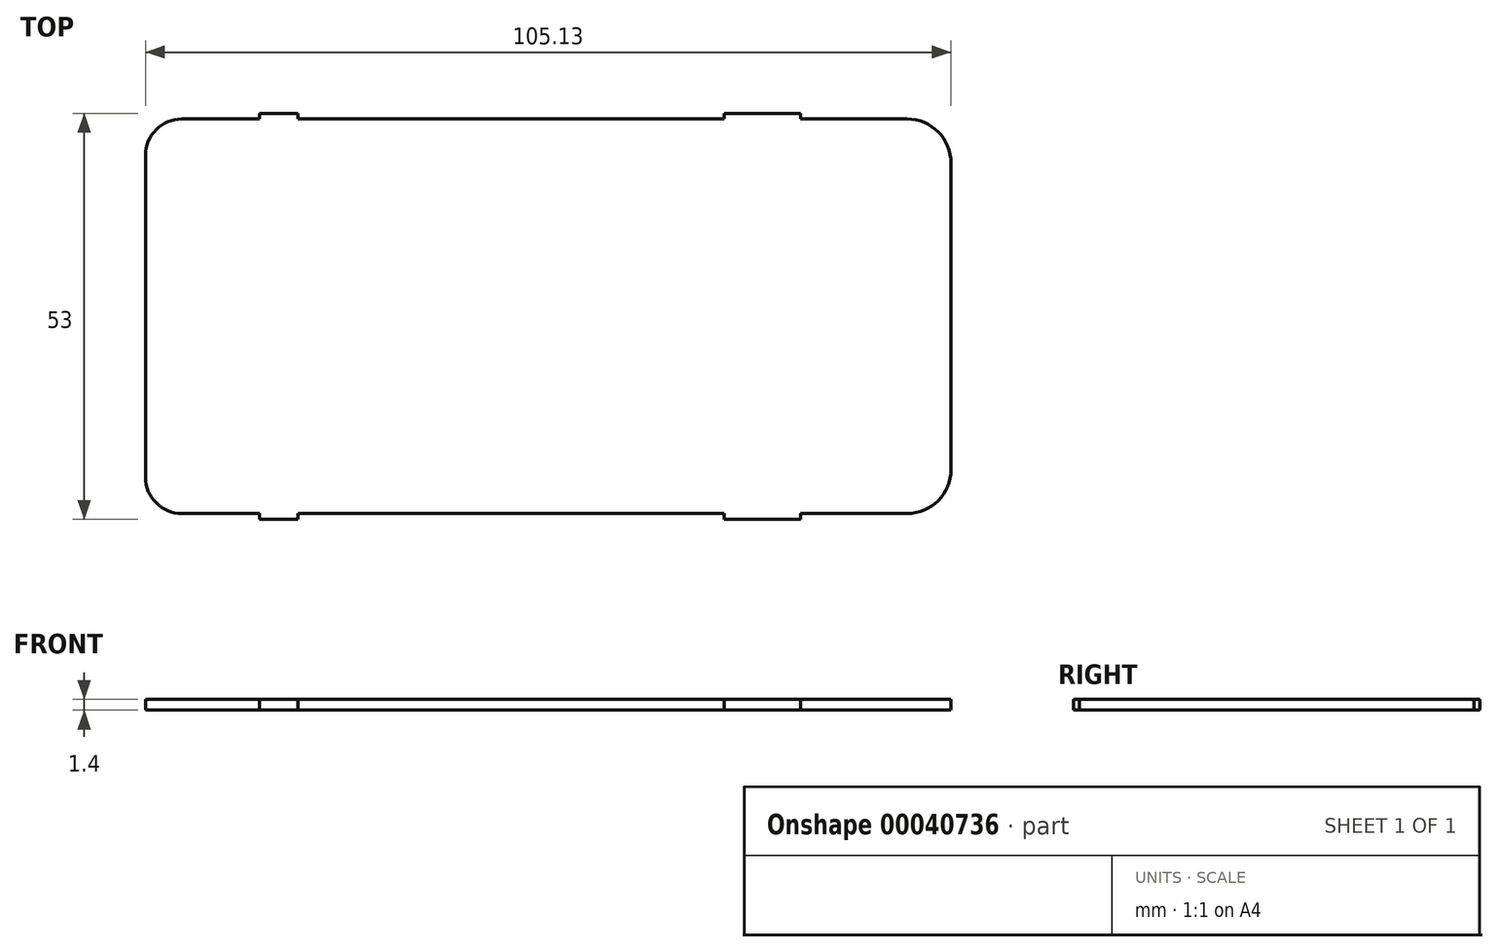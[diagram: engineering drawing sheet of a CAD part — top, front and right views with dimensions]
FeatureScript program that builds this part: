
annotation { "Feature Type Name" : "Feature", "Feature Type Description" : "" }
export const myFeature = defineFeature(function(context is Context, id is Id, definition is map)
    precondition{}
    {
        {
            var Q0;
            Q0=qCreatedBy(makeId("Top.planeOp"),FACE);
            var sketch = newSketch(context, id + "F0", { "sketchPlane" : qUnion([Q0])});
            skLineSegment(sketch, "E0", {"start": v(-46.45, 26.5) * mm, "end": v(-46.45, 25) * mm});
            skLineSegment(sketch, "E1", {"start": v(-46.45, -26.5) * mm, "end": v(-46.45, -25) * mm});
            skLineSegment(sketch, "E2", {"start": v(-50.45, -21) * mm, "end": v(-51.95, -21) * mm});
            skLineSegment(sketch, "E3", {"start": v(-50.45, 21) * mm, "end": v(-51.95, 21) * mm});
            skLineSegment(sketch, "E4", {"start": v(48.18, 25) * mm, "end": v(48.18, 26.5) * mm});
            skLineSegment(sketch, "E5", {"start": v(53.18, 20) * mm, "end": v(54.68, 20) * mm});
            skLineSegment(sketch, "E6", {"start": v(54.68, -20) * mm, "end": v(53.18, -20) * mm});
            skLineSegment(sketch, "E7", {"start": v(48.18, -26.5) * mm, "end": v(48.18, -25) * mm});
            skLineSegment(sketch, "E8", {"start": v(-46.45, -25.75) * mm, "end": v(48.18, -25.75) * mm});
            skLineSegment(sketch, "E9", {"start": v(-46.45, 25.75) * mm, "end": v(48.18, 25.75) * mm});
            skLineSegment(sketch, "E10", {"start": v(-51.2, 21) * mm, "end": v(-51.2, -21) * mm});
            skArc(sketch, "E11", {"start": v(-51.2, 21) * mm, "mid": v(-49.81, 24.36) * mm, "end": v(-46.45, 25.75) * mm});
            skArc(sketch, "E12", {"start": v(-51.2, -21) * mm, "mid": v(-49.81, -24.36) * mm, "end": v(-46.45, -25.75) * mm});
            skLineSegment(sketch, "E13", {"start": v(53.93, 20) * mm, "end": v(53.93, -20) * mm});
            skArc(sketch, "E14", {"start": v(48.18, -25.75) * mm, "mid": v(52.24, -24.07) * mm, "end": v(53.93, -20) * mm});
            skArc(sketch, "E15", {"start": v(53.93, 20) * mm, "mid": v(52.24, 24.07) * mm, "end": v(48.18, 25.75) * mm});
            skLineSegment(sketch, "E16", {"start": v(-36.31, 26.5) * mm, "end": v(-36.31, -26.5) * mm});
            skLineSegment(sketch, "E17", {"start": v(-36.31, -26.5) * mm, "end": v(-31.31, -26.5) * mm});
            skLineSegment(sketch, "E18", {"start": v(-31.31, -26.5) * mm, "end": v(-31.31, 26.5) * mm});
            skLineSegment(sketch, "E19", {"start": v(-31.31, 26.5) * mm, "end": v(-36.31, 26.5) * mm});
            skLineSegment(sketch, "E20", {"start": v(24.3, 26.5) * mm, "end": v(24.3, -26.5) * mm});
            skLineSegment(sketch, "E21", {"start": v(24.3, -26.5) * mm, "end": v(34.3, -26.5) * mm});
            skLineSegment(sketch, "E22", {"start": v(34.3, -26.5) * mm, "end": v(34.3, 26.5) * mm});
            skLineSegment(sketch, "E23", {"start": v(34.3, 26.5) * mm, "end": v(24.3, 26.5) * mm});
            skSolve(sketch);
        }
        {
            var Q0;
            {var subQ3=sQuery(id+"F0.wireOp",EDGE,"E8");var subQ5=sQuery(id+"F0.wireOp",EDGE,"E18");var subQ7=makeQuery(id+"F0.imprint","INTERSECT",VERTEX,{"derivedFrom":[subQ3,subQ5]});Q0=makeQuery(id+"F0.imprint","IMPRINT",FACE,{"disambiguationData":[TD([[makeQuery(id+"F0.imprint","IMPRINT",EDGE,{"disambiguationData":[TD([[subQ7,-1.0]])],"derivedFrom":subQ3}),1.0]])]});}
            var Q1;
            {var subQ3=sQuery(id+"F0.wireOp",EDGE,"E8");var subQ5=sQuery(id+"F0.wireOp",EDGE,"E16");var subQ7=makeQuery(id+"F0.imprint","INTERSECT",VERTEX,{"derivedFrom":[subQ3,subQ5]});Q1=makeQuery(id+"F0.imprint","IMPRINT",FACE,{"disambiguationData":[TD([[makeQuery(id+"F0.imprint","IMPRINT",EDGE,{"disambiguationData":[TD([[subQ7,-1.0]])],"derivedFrom":subQ3}),1.0]])]});}
            var Q2;
            Q2=makeQuery(id+"F0.imprint","IMPRINT",FACE,{"disambiguationData":[TD([[makeQuery(id+"F0.imprint","IMPRINT",EDGE,{"derivedFrom":sQuery(id+"F0.wireOp",EDGE,"E10")}),1.0]])]});
            var Q3;
            {var subQ3=sQuery(id+"F0.wireOp",EDGE,"E8");var subQ5=sQuery(id+"F0.wireOp",EDGE,"E20");var subQ7=makeQuery(id+"F0.imprint","INTERSECT",VERTEX,{"derivedFrom":[subQ3,subQ5]});Q3=makeQuery(id+"F0.imprint","IMPRINT",FACE,{"disambiguationData":[TD([[makeQuery(id+"F0.imprint","IMPRINT",EDGE,{"disambiguationData":[TD([[subQ7,-1.0]])],"derivedFrom":subQ3}),1.0]])]});}
            var Q4;
            Q4=makeQuery(id+"F0.imprint","IMPRINT",FACE,{"disambiguationData":[TD([[makeQuery(id+"F0.imprint","IMPRINT",EDGE,{"derivedFrom":sQuery(id+"F0.wireOp",EDGE,"E13")}),-1.0]])]});
            var Q5;
            {var subQ3=sQuery(id+"F0.wireOp",EDGE,"E21");Q5=makeQuery(id+"F0.imprint","IMPRINT",FACE,{"disambiguationData":[TD([[makeQuery(id+"F0.imprint","IMPRINT",EDGE,{"derivedFrom":subQ3}),1.0]])]});}
            var Q6;
            {var subQ0=sQuery(id+"F0.wireOp",EDGE,"E23");Q6=makeQuery(id+"F0.imprint","IMPRINT",FACE,{"disambiguationData":[TD([[makeQuery(id+"F0.imprint","IMPRINT",EDGE,{"derivedFrom":subQ0}),1.0]])]});}
            var Q7;
            {var subQ0=sQuery(id+"F0.wireOp",EDGE,"E19");Q7=makeQuery(id+"F0.imprint","IMPRINT",FACE,{"disambiguationData":[TD([[makeQuery(id+"F0.imprint","IMPRINT",EDGE,{"derivedFrom":subQ0}),1.0]])]});}
            var Q8;
            {var subQ3=sQuery(id+"F0.wireOp",EDGE,"E17");Q8=makeQuery(id+"F0.imprint","IMPRINT",FACE,{"disambiguationData":[TD([[makeQuery(id+"F0.imprint","IMPRINT",EDGE,{"derivedFrom":subQ3}),1.0]])]});}
            extrude(context, id + "F1", {"entities" : qUnion([Q0, Q1, Q2, Q3, Q4, Q5, Q6, Q7, Q8]), "depth" : 1.4 * mm});
        }
    });
